# Revit family: Toilet-Wall_Mount-KOHLER-Veil-K-31539_1
name_source: partatom
category: Plumbing Fixtures
units: mm (PartAtom-declared; Revit-internal decimal feet)

## family parameters
Cut with Voids When Loaded = No
Host = Face
Maintain Annotation Orientation = No
OmniClass Number = 23.31.19.00
OmniClass Title = Toilets
Part Type = Normal
Room Calculation Point = No
Round Connector Dimension = Use Diameter
Shared = No

## types (5) — shared parameters
ADA Compliant = No
Assembly Code = D2010100
CW Connection = Yes
Cold Water Inlet = Cold Water Inlet
Date Modified = 02/02/2022
Default Elevation = 0"
Description = WALL HUNG EB BOWL
Flow Rate = 0 GPM
Flush Rate- GPF = GPF
Flush Rate- LPF = LPF
HW Connection = No
Height = 14 15/16"
Hot Water Inlet = Hot Water Inlet
Length = 21 13/16"
Manufacturer = KOHLER Co.
Master Format 2014 = 22 42 13.13
Master Format 2014 Name = Residential Water Closets
Material = Vitreous China
Pressure = 0.00 psi
Product Documentation Link = https://www.us.kohler.com
Product Name = Veil
Product Page URL = http://www.us.kohler.com
Seat Included = Yes
URL = https://www.us.kohler.com
Vent Connection = No
Waste Connection = Yes
Waste Water Outlet = Waste Water Outlet
WaterSense Certified = No
Width = 15 3/16"

## per-type parameters (varying)
| type | Finish | Model | Type |
| 0-White | Kohler-Vitreous_China-0-White | K-31539-0 | 1 |
| 7-Black Black | Kohler-Vitreous_China-7-Black_Black | K-31539-7 | 2 |
| 96-Biscuit | Kohler-Vitreous_China-96-Biscuit | K-31539-96 | 3 |
| NY-Dune | Kohler-Vitreous_China-NY-Dune | K-31539-NY | 4 |
| 58-Thunder Grey | Kohler-Vitreous_China-58-Thunder_Grey | K-31539-58 | 5 |

## geometry (parser evidence)
native form markers: Sweep x5
no freeform markers — native parametric forms only
